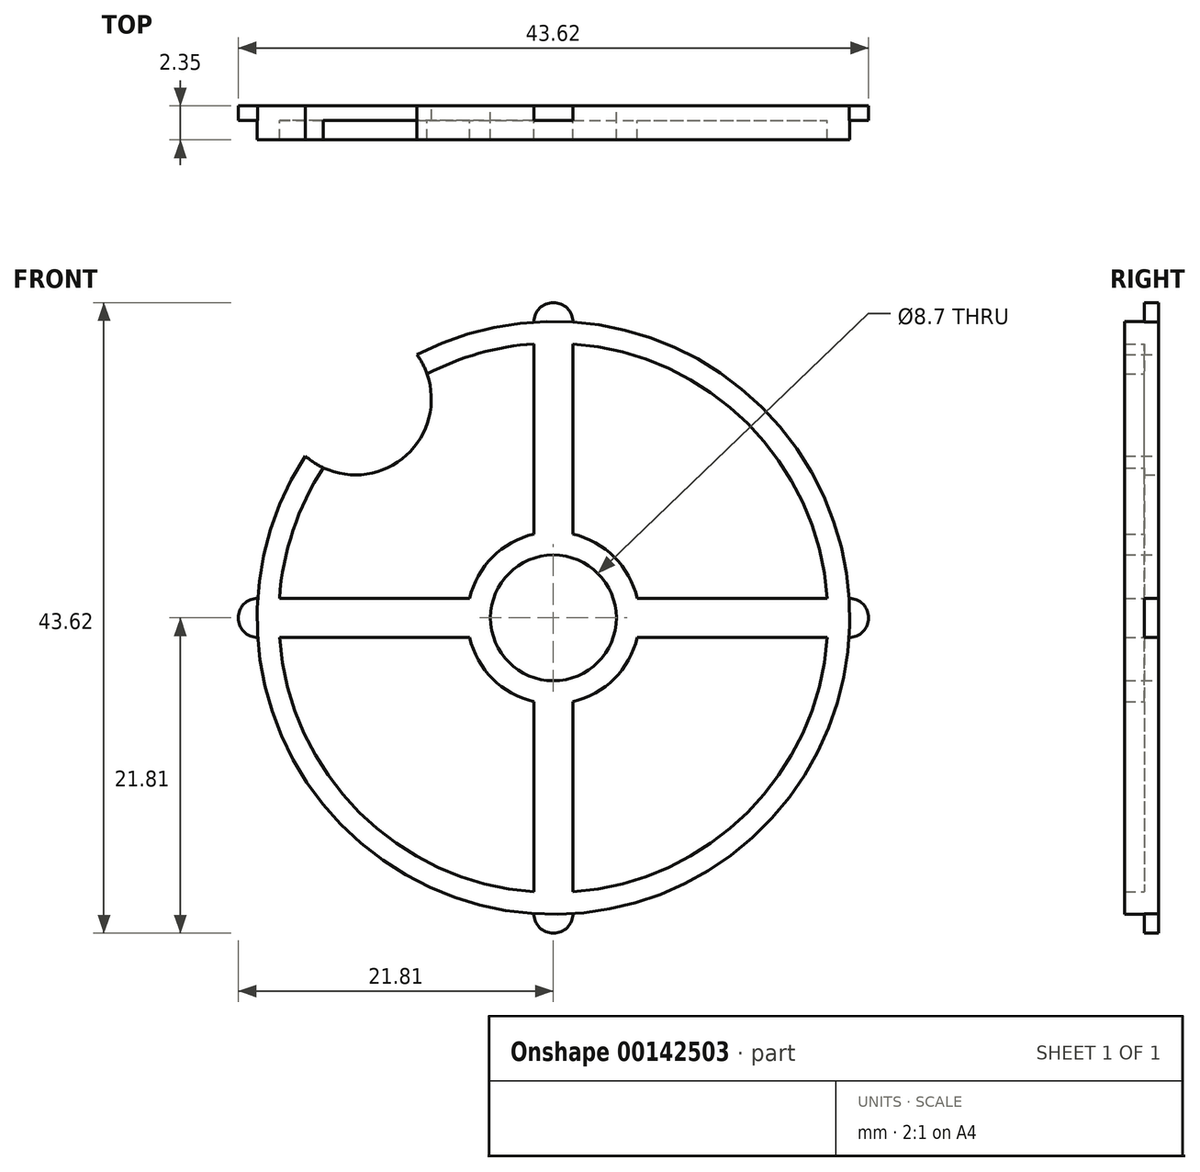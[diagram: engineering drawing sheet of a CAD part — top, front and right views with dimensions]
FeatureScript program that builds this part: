
annotation { "Feature Type Name" : "Feature", "Feature Type Description" : "" }
export const myFeature = defineFeature(function(context is Context, id is Id, definition is map)
    precondition{}
    {
        {
            var Q0;
            Q0=qCreatedBy(makeId("Front.planeOp"),FACE);
            var sketch = newSketch(context, id + "F0", { "sketchPlane" : qUnion([Q0])});
            skCircle(sketch, "E0", {"center": v(0, 0) * mm, "radius": 19 * mm});
            skCircle(sketch, "E1", {"center": v(0, 0) * mm, "radius": 5.95 * mm});
            skLineSegment(sketch, "E2", {"start": v(-1.35, 5.8) * mm, "end": v(-1.35, 18.95) * mm});
            skLineSegment(sketch, "E3", {"start": v(1.35, 5.8) * mm, "end": v(1.35, 18.95) * mm});
            skLineSegment(sketch, "E4", {"start": v(-1.35, -5.8) * mm, "end": v(-1.35, -18.95) * mm});
            skLineSegment(sketch, "E5", {"start": v(1.35, -5.8) * mm, "end": v(1.35, -18.95) * mm});
            skLineSegment(sketch, "E6", {"start": v(-5.8, 1.35) * mm, "end": v(-18.95, 1.35) * mm});
            skLineSegment(sketch, "E7", {"start": v(-5.8, -1.35) * mm, "end": v(-18.95, -1.35) * mm});
            skLineSegment(sketch, "E8", {"start": v(5.8, 1.35) * mm, "end": v(18.95, 1.35) * mm});
            skLineSegment(sketch, "E9", {"start": v(5.8, -1.35) * mm, "end": v(18.95, -1.35) * mm});
            skCircle(sketch, "E10", {"center": v(0, 0) * mm, "radius": 20.5 * mm});
            skCircle(sketch, "E11", {"center": v(0, 0) * mm, "radius": 4.35 * mm});
            skArc(sketch, "E12", {"start": v(-17.17, 11.2) * mm, "mid": v(-10.17, 11.24) * mm, "end": v(-9.43, 18.2) * mm});
            skLineSegment(sketch, "E13", {"start": v(-1.35, 18.95) * mm, "end": v(-1.35, 20.46) * mm, "construction": true});
            skLineSegment(sketch, "E14", {"start": v(1.35, 18.95) * mm, "end": v(1.35, 20.46) * mm, "construction": true});
            skArc(sketch, "E15", {"start": v(1.35, 20.46) * mm, "mid": v(0, 21.8) * mm, "end": v(-1.35, 20.46) * mm});
            skLineSegment(sketch, "E16", {"start": v(-18.95, 1.35) * mm, "end": v(-20.46, 1.35) * mm, "construction": true});
            skLineSegment(sketch, "E17", {"start": v(-18.95, -1.35) * mm, "end": v(-20.46, -1.35) * mm, "construction": true});
            skArc(sketch, "E18", {"start": v(-20.46, 1.35) * mm, "mid": v(-21.8, 0) * mm, "end": v(-20.46, -1.35) * mm});
            skLineSegment(sketch, "E19", {"start": v(-1.35, -18.95) * mm, "end": v(-1.35, -20.46) * mm, "construction": true});
            skLineSegment(sketch, "E20", {"start": v(1.35, -18.95) * mm, "end": v(1.35, -20.46) * mm, "construction": true});
            skArc(sketch, "E21", {"start": v(-1.35, -20.46) * mm, "mid": v(0, -21.8) * mm, "end": v(1.35, -20.46) * mm});
            skLineSegment(sketch, "E22", {"start": v(18.95, 1.35) * mm, "end": v(20.46, 1.35) * mm, "construction": true});
            skLineSegment(sketch, "E23", {"start": v(18.95, -1.35) * mm, "end": v(20.46, -1.35) * mm, "construction": true});
            skArc(sketch, "E24", {"start": v(20.46, -1.35) * mm, "mid": v(21.8, 0) * mm, "end": v(20.46, 1.35) * mm});
            skSolve(sketch);
        }
        {
            var Q0;
            {var subQ4=sQuery(id+"F0.wireOp",EDGE,"E0");var subQ7=makeQuery(id+"F0.imprint","INTERSECT",VERTEX,{"derivedFrom":[subQ4,sQuery(id+"F0.wireOp",EDGE,"E3")]});Q0=makeQuery(id+"F0.imprint","IMPRINT",FACE,{"disambiguationData":[TD([[makeQuery(id+"F0.imprint","IMPRINT",EDGE,{"disambiguationData":[TD([[subQ7,1.0]])],"derivedFrom":subQ4}),-1.0]])]});}
            var Q1;
            {var subQ0=sQuery(id+"F0.wireOp",EDGE,"E4");Q1=makeQuery(id+"F0.imprint","IMPRINT",FACE,{"disambiguationData":[TD([[makeQuery(id+"F0.imprint","IMPRINT",EDGE,{"derivedFrom":subQ0}),1.0]])]});}
            var Q2;
            {var subQ0=sQuery(id+"F0.wireOp",EDGE,"E8");Q2=makeQuery(id+"F0.imprint","IMPRINT",FACE,{"disambiguationData":[TD([[makeQuery(id+"F0.imprint","IMPRINT",EDGE,{"derivedFrom":subQ0}),-1.0]])]});}
            var Q3;
            {var subQ0=sQuery(id+"F0.wireOp",EDGE,"E6");Q3=makeQuery(id+"F0.imprint","IMPRINT",FACE,{"disambiguationData":[TD([[makeQuery(id+"F0.imprint","IMPRINT",EDGE,{"derivedFrom":subQ0}),1.0]])]});}
            var Q4;
            {var subQ0=sQuery(id+"F0.wireOp",EDGE,"E2");Q4=makeQuery(id+"F0.imprint","IMPRINT",FACE,{"disambiguationData":[TD([[makeQuery(id+"F0.imprint","IMPRINT",EDGE,{"derivedFrom":subQ0}),-1.0]])]});}
            var Q5;
            {var subQ0=sQuery(id+"F0.wireOp",EDGE,"JQplNzLy-MDn4-o3jD-dyHa-r76O8bGRBZya");Q5=makeQuery(id+"F0.imprint","IMPRINT",FACE,{"disambiguationData":[TD([[makeQuery(id+"F0.imprint","IMPRINT",EDGE,{"derivedFrom":subQ0}),1.0]])]});}
            var Q6;
            {var subQ0=sQuery(id+"F0.wireOp",EDGE,"iP1EGVPw-j7wL-WCFN-5Kgd-LL717Ze5B378");Q6=makeQuery(id+"F0.imprint","IMPRINT",FACE,{"disambiguationData":[TD([[makeQuery(id+"F0.imprint","IMPRINT",EDGE,{"derivedFrom":subQ0}),1.0]])]});}
            var Q7;
            {var subQ0=sQuery(id+"F0.wireOp",EDGE,"CEaXaM09-qpk9-WgmC-VFXw-WiOaJCkjnFe9");Q7=makeQuery(id+"F0.imprint","IMPRINT",FACE,{"disambiguationData":[TD([[makeQuery(id+"F0.imprint","IMPRINT",EDGE,{"derivedFrom":subQ0}),1.0]])]});}
            var Q8;
            {var subQ0=sQuery(id+"F0.wireOp",EDGE,"5ZXZNUGm-eNXA-uQi5-Vss4-XkvxrCQkCZnC");Q8=makeQuery(id+"F0.imprint","IMPRINT",FACE,{"disambiguationData":[TD([[makeQuery(id+"F0.imprint","IMPRINT",EDGE,{"derivedFrom":subQ0}),1.0]])]});}
            var Q9;
            {var subQ0=sQuery(id+"F0.wireOp",EDGE,"E1");var subQ4=makeQuery(id+"F0.imprint","INTERSECT",VERTEX,{"derivedFrom":[subQ0,sQuery(id+"F0.wireOp",EDGE,"E3")]});Q9=makeQuery(id+"F0.imprint","IMPRINT",FACE,{"disambiguationData":[TD([[makeQuery(id+"F0.imprint","IMPRINT",EDGE,{"disambiguationData":[TD([[subQ4,1.0]])],"derivedFrom":subQ0}),1.0]])]});}
            extrude(context, id + "F1", {"entities" : qUnion([Q0, Q1, Q2, Q3, Q4, Q5, Q6, Q7, Q8, Q9]), "depth" : 2.35 * mm});
        }
        {
            var Q0;
            {var subQ0=sQuery(id+"F0.wireOp",EDGE,"E2");Q0=makeQuery(id+"F0.imprint","IMPRINT",FACE,{"disambiguationData":[TD([[makeQuery(id+"F0.imprint","IMPRINT",EDGE,{"derivedFrom":subQ0}),1.0]])]});}
            var Q1;
            {var subQ0=sQuery(id+"F0.wireOp",EDGE,"E5");Q1=makeQuery(id+"F0.imprint","IMPRINT",FACE,{"disambiguationData":[TD([[makeQuery(id+"F0.imprint","IMPRINT",EDGE,{"derivedFrom":subQ0}),1.0]])]});}
            var Q2;
            {var subQ0=sQuery(id+"F0.wireOp",EDGE,"E3");Q2=makeQuery(id+"F0.imprint","IMPRINT",FACE,{"disambiguationData":[TD([[makeQuery(id+"F0.imprint","IMPRINT",EDGE,{"derivedFrom":subQ0}),-1.0]])]});}
            var Q3;
            {var subQ0=sQuery(id+"F0.wireOp",EDGE,"E4");Q3=makeQuery(id+"F0.imprint","IMPRINT",FACE,{"disambiguationData":[TD([[makeQuery(id+"F0.imprint","IMPRINT",EDGE,{"derivedFrom":subQ0}),-1.0]])]});}
            var Q4;
            {var subQ0=sQuery(id+"F0.wireOp",EDGE,"E18");Q4=makeQuery(id+"F0.imprint","IMPRINT",FACE,{"disambiguationData":[TD([[makeQuery(id+"F0.imprint","IMPRINT",EDGE,{"derivedFrom":subQ0}),1.0]])]});}
            var Q5;
            {var subQ0=sQuery(id+"F0.wireOp",EDGE,"E21");Q5=makeQuery(id+"F0.imprint","IMPRINT",FACE,{"disambiguationData":[TD([[makeQuery(id+"F0.imprint","IMPRINT",EDGE,{"derivedFrom":subQ0}),1.0]])]});}
            var Q6;
            {var subQ0=sQuery(id+"F0.wireOp",EDGE,"E24");Q6=makeQuery(id+"F0.imprint","IMPRINT",FACE,{"disambiguationData":[TD([[makeQuery(id+"F0.imprint","IMPRINT",EDGE,{"derivedFrom":subQ0}),1.0]])]});}
            var Q7;
            {var subQ0=sQuery(id+"F0.wireOp",EDGE,"E15");Q7=makeQuery(id+"F0.imprint","IMPRINT",FACE,{"disambiguationData":[TD([[makeQuery(id+"F0.imprint","IMPRINT",EDGE,{"derivedFrom":subQ0}),1.0]])]});}
            extrude(context, id + "F2", {"entities" : qUnion([Q0, Q1, Q2, Q3, Q4, Q5, Q6, Q7]), "operationType" : NewBodyOperationType.ADD, "depth" : 1 * mm});
        }
        {
            var Q0;
            Q0 = qSketchRegion(id + "F0", true);
            extrude(context, id + "F3", {"entities" : qUnion([Q0]), "operationType" : NewBodyOperationType.REMOVE, "oppositeDirection" : true, "depth" : 25 * mm});
        }
    });
